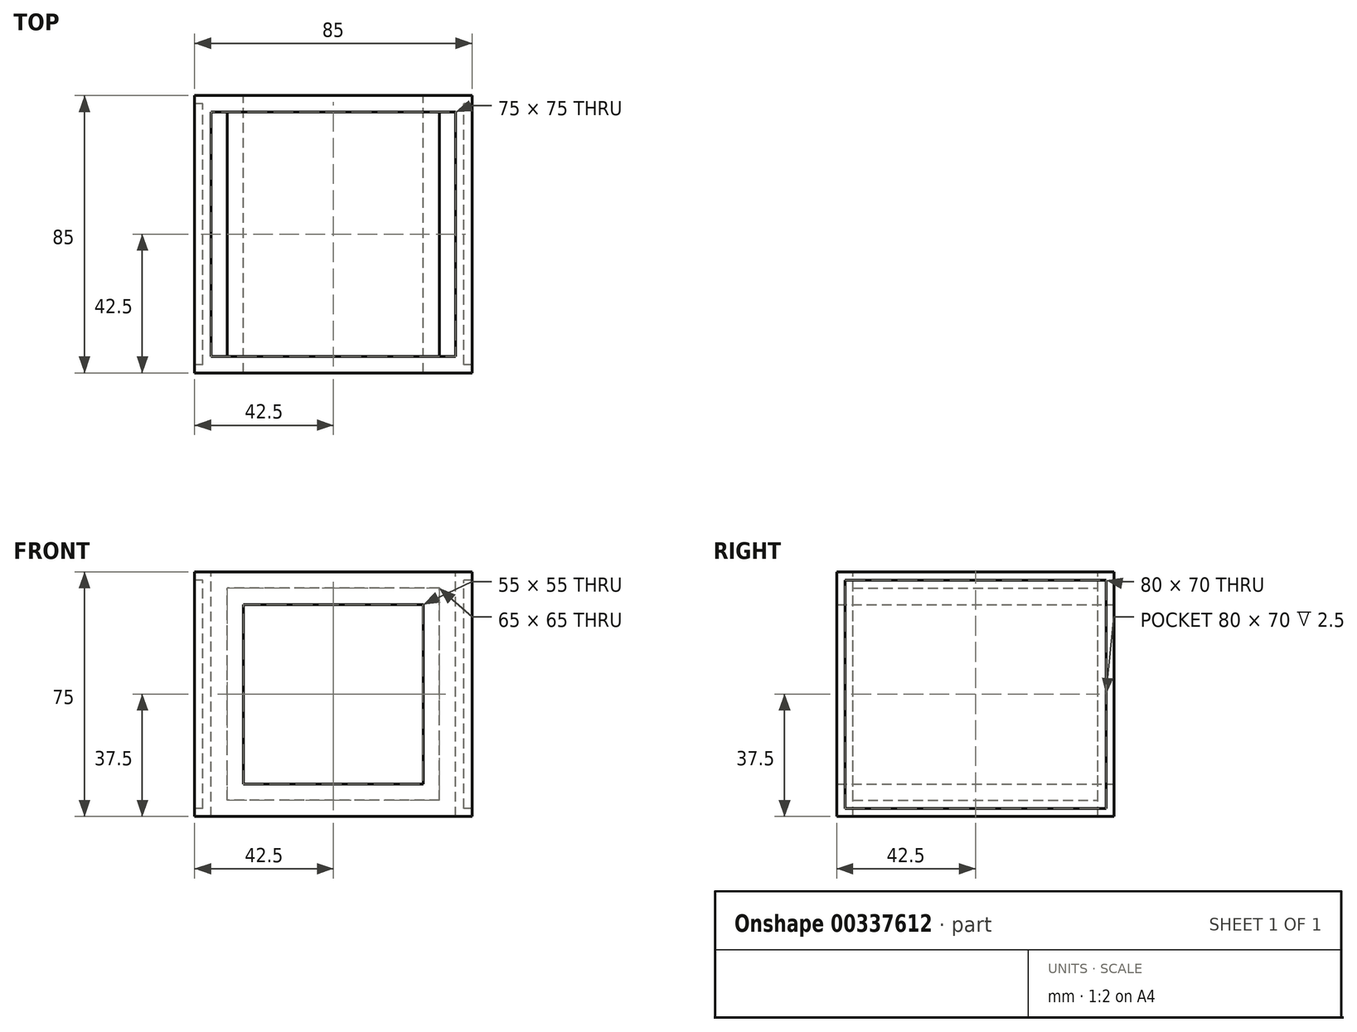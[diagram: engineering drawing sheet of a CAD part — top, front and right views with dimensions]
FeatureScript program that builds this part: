
annotation { "Feature Type Name" : "Feature", "Feature Type Description" : "" }
export const myFeature = defineFeature(function(context is Context, id is Id, definition is map)
    precondition{}
    {
        {
            var Q0;
            Q0=qCreatedBy(makeId("Front.planeOp"),FACE);
            var sketch = newSketch(context, id + "F0", { "sketchPlane" : qUnion([Q0])});
            skLineSegment(sketch, "E0.bottom", {"start": v(37.5, -37.5) * mm, "end": v(-37.5, -37.5) * mm});
            skLineSegment(sketch, "E0.top", {"start": v(37.5, 37.5) * mm, "end": v(-37.5, 37.5) * mm});
            skLineSegment(sketch, "E0.left", {"start": v(37.5, -37.5) * mm, "end": v(37.5, 37.5) * mm});
            skLineSegment(sketch, "E0.right", {"start": v(-37.5, -37.5) * mm, "end": v(-37.5, 37.5) * mm});
            skPoint(sketch, "E0.middle", {"position": v(0, 0) * mm});
            skSolve(sketch);
        }
        {
            var Q0;
            Q0 = qSketchRegion(id + "F0", true);
            extrude(context, id + "F1", {"entities" : qUnion([Q0]), "depth" : 75 * mm});
        }
        {
            var Q0;
            Q0=makeQuery(id+"F1.opExtrude","CAP_FACE",FACE,{"disambiguationData":[OSD([sQuery(id+"F0.wireOp",EDGE,"E0.bottom"),sQuery(id+"F0.wireOp",EDGE,"E0.top"),sQuery(id+"F0.wireOp",EDGE,"E0.left"),sQuery(id+"F0.wireOp",EDGE,"E0.right")])],"isStart":false});
            var Q1;
            Q1=makeQuery(id+"F1.opExtrude","CAP_FACE",FACE,{"disambiguationData":[OSD([sQuery(id+"F0.wireOp",EDGE,"E0.bottom"),sQuery(id+"F0.wireOp",EDGE,"E0.top"),sQuery(id+"F0.wireOp",EDGE,"E0.left"),sQuery(id+"F0.wireOp",EDGE,"E0.right")])],"isStart":true});
            shell(context, id + "F2", {"entities" : qUnion([Q0, Q1]), "thickness" : 5 * mm});
        }
        {
            var Q0;
            Q0=makeQuery(id+"F1.opExtrude","SWEPT_FACE",FACE,{"disambiguationData":[OSD([sQuery(id+"F0.wireOp",EDGE,"E0.top")])]});
            var Q1;
            Q1=makeQuery(id+"F1.opExtrude","SWEPT_FACE",FACE,{"disambiguationData":[OSD([sQuery(id+"F0.wireOp",EDGE,"E0.bottom")])]});
            shell(context, id + "F3", {"entities" : qUnion([Q0, Q1]), "thickness" : 5 * mm, "oppositeDirection" : true});
        }
        {
            var Q0;
            Q0=makeQuery(id+"F1.opExtrude","SWEPT_FACE",FACE,{"disambiguationData":[OSD([sQuery(id+"F0.wireOp",EDGE,"E0.right")])]});
            var Q1;
            Q1=makeQuery(id+"F1.opExtrude","SWEPT_FACE",FACE,{"disambiguationData":[OSD([sQuery(id+"F0.wireOp",EDGE,"E0.left")])]});
            shell(context, id + "F4", {"entities" : qUnion([Q0, Q1]), "thickness" : 2.5 * mm});
        }
    });
